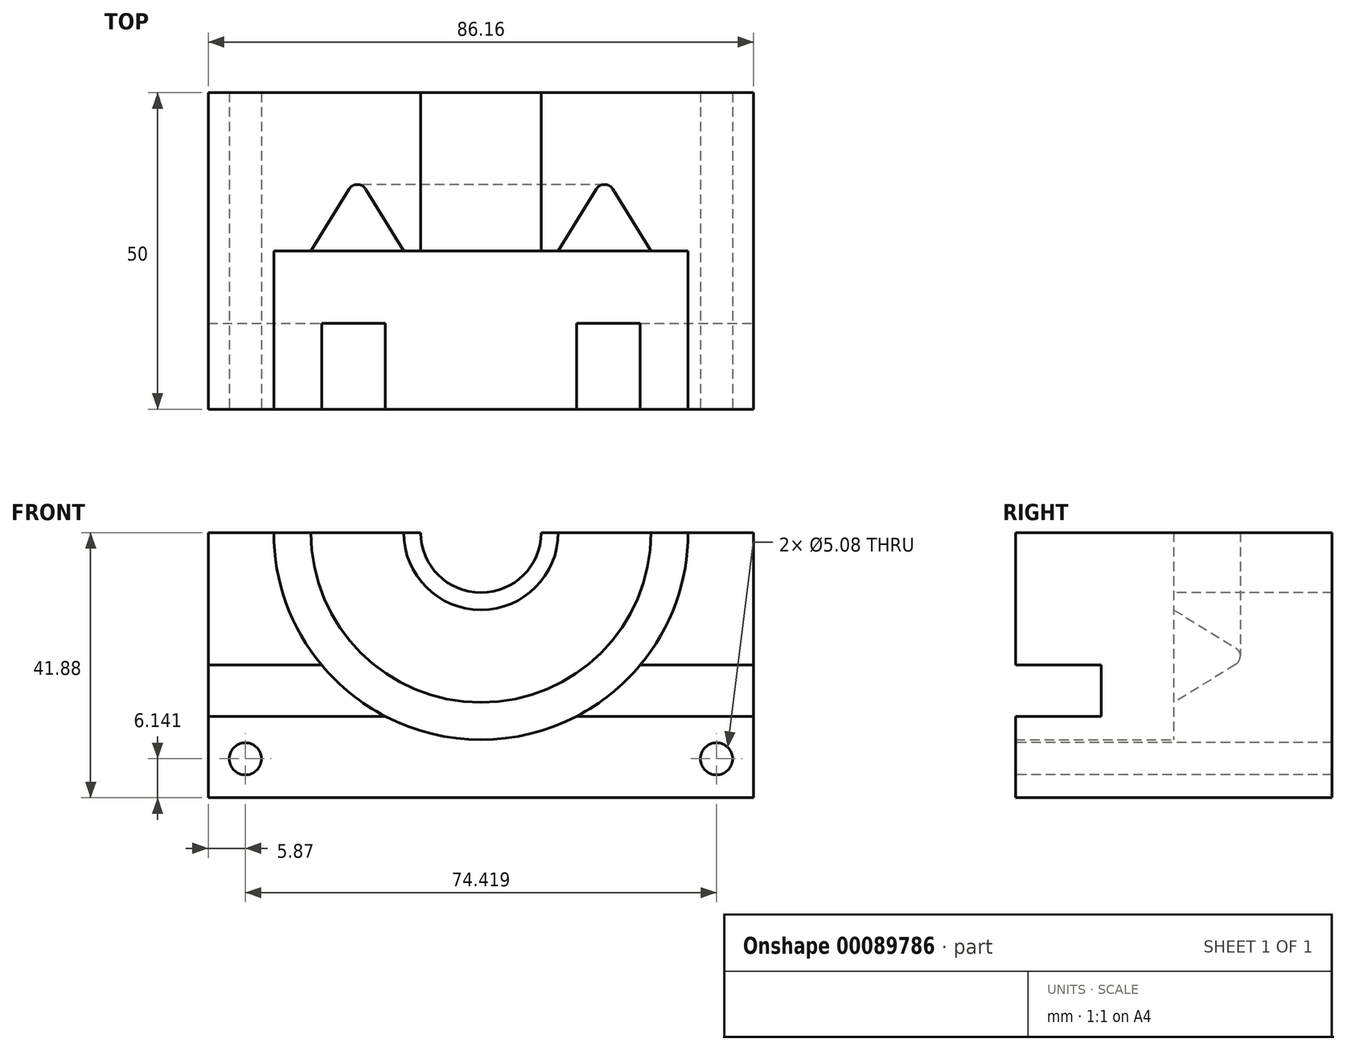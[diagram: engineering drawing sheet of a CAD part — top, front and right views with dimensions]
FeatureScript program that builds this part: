
annotation { "Feature Type Name" : "Feature", "Feature Type Description" : "" }
export const myFeature = defineFeature(function(context is Context, id is Id, definition is map)
    precondition{}
    {
        {
            var Q0;
            Q0=qCreatedBy(makeId("Front.planeOp"),FACE);
            var sketch = newSketch(context, id + "F0", { "sketchPlane" : qUnion([Q0])});
            skLineSegment(sketch, "E0", {"start": v(-43.08, 0) * mm, "end": v(0, 0) * mm});
            skLineSegment(sketch, "E1", {"start": v(0, 0) * mm, "end": v(43.08, 0) * mm});
            skLineSegment(sketch, "E2", {"start": v(43.08, 0) * mm, "end": v(43.08, 41.88) * mm});
            skLineSegment(sketch, "E3.MirrorCS", {"start": v(-43.08, 0) * mm, "end": v(-43.08, 41.88) * mm});
            skLineSegment(sketch, "E4", {"start": v(-43.08, 41.88) * mm, "end": v(43.08, 41.88) * mm});
            skSolve(sketch);
        }
        {
            var Q0;
            Q0=makeQuery(id+"F0.imprint","IMPRINT",FACE,{"disambiguationData":[TD([[makeQuery(id+"F0.imprint","IMPRINT",EDGE,{"derivedFrom":sQuery(id+"F0.wireOp",EDGE,"E0")}),1.0]])]});
            extrude(context, id + "F1", {"entities" : qUnion([Q0]), "endBound" : BoundingType.SYMMETRIC, "depth" : 50 * mm});
        }
        {
            var Q0;
            Q0=makeQuery(id+"F1.opExtrude","SWEPT_FACE",FACE,{"disambiguationData":[OSD([sQuery(id+"F0.wireOp",EDGE,"E4")])]});
            var sketch = newSketch(context, id + "F2", { "sketchPlane" : qUnion([Q0])});
            skLineSegment(sketch, "E5", {"start": v(-26.85, 0) * mm, "end": v(-19.53, 11.87) * mm});
            skLineSegment(sketch, "E6", {"start": v(-19.53, 11.87) * mm, "end": v(-12.2, 0) * mm});
            skLineSegment(sketch, "E7", {"start": v(-12.2, 0) * mm, "end": v(-26.85, 0) * mm});
            skLineSegment(sketch, "E8", {"start": v(0, 25) * mm, "end": v(0, -25) * mm});
            skSolve(sketch);
        }
        {
            var Q0;
            Q0=makeQuery(id+"F2.imprint","IMPRINT",FACE,{"disambiguationData":[TD([[makeQuery(id+"F2.imprint","IMPRINT",EDGE,{"derivedFrom":sQuery(id+"F2.wireOp",EDGE,"E5")}),-1.0]])]});
            var Q1;
            Q1=sQuery(id+"F2.wireOp",EDGE,"E8");
            revolve(context, id + "F3", {"operationType" : NewBodyOperationType.REMOVE, "entities" : qUnion([Q0]), "axis" : qUnion([Q1]), "revolveType" : RevolveType.FULL, "oppositeDirection" : true});
        }
        {
            var Q0;
            Q0=makeQuery(id+"F1.opExtrude","SWEPT_FACE",FACE,{"disambiguationData":[OSD([sQuery(id+"F0.wireOp",EDGE,"E4")])]});
            var sketch = newSketch(context, id + "F4", { "sketchPlane" : qUnion([Q0])});
            skLineSegment(sketch, "E9", {"start": v(-32.73, 0) * mm, "end": v(-32.73, -25) * mm});
            skLineSegment(sketch, "E10", {"start": v(-32.73, -25) * mm, "end": v(0, -25) * mm});
            skLineSegment(sketch, "E11", {"start": v(0, -25) * mm, "end": v(0, 0) * mm});
            skLineSegment(sketch, "E12", {"start": v(0, 0) * mm, "end": v(-32.73, 0) * mm});
            skSolve(sketch);
        }
        {
            var Q0;
            Q0 = qSketchRegion(id + "F4", true);
            var Q1;
            Q1=sQuery(id+"F4.wireOp",EDGE,"E11");
            revolve(context, id + "F5", {"operationType" : NewBodyOperationType.REMOVE, "entities" : qUnion([Q0]), "axis" : qUnion([Q1]), "revolveType" : RevolveType.FULL, "oppositeDirection" : true});
        }
        {
            var Q0;
            Q0=makeQuery(id+"F3.boolean.opBoolean","COPY",EDGE,{"derivedFrom":makeQuery(id+"F3.opRevolve","SWEPT_EDGE",EDGE,{"disambiguationData":[OSD([sQuery(id+"F2.wireOp",EDGE,"E5"),sQuery(id+"F2.wireOp",EDGE,"E6")])]})});
            fillet(context, id + "F6", {"entities" : qUnion([Q0]), "radius" : 1.52 * mm, "tangentPropagation" : true, "allowEdgeOverflow" : false});
        }
        {
            var Q0;
            Q0=makeQuery(id+"F1.opExtrude","SWEPT_FACE",FACE,{"disambiguationData":[OSD([sQuery(id+"F0.wireOp",EDGE,"E2")])]});
            var sketch = newSketch(context, id + "F7", { "sketchPlane" : qUnion([Q0])});
            skLineSegment(sketch, "E13", {"start": v(-25, 20.94) * mm, "end": v(-11.47, 20.94) * mm});
            skLineSegment(sketch, "E14", {"start": v(-11.47, 20.94) * mm, "end": v(-11.47, 12.85) * mm});
            skLineSegment(sketch, "E15", {"start": v(-11.47, 12.85) * mm, "end": v(-25, 12.85) * mm});
            skLineSegment(sketch, "E16", {"start": v(-25, 12.85) * mm, "end": v(-25, 20.94) * mm});
            skSolve(sketch);
        }
        {
            var Q0;
            Q0 = qSketchRegion(id + "F7", true);
            extrude(context, id + "F8", {"entities" : qUnion([Q0]), "operationType" : NewBodyOperationType.REMOVE, "endBound" : BoundingType.THROUGH_ALL, "oppositeDirection" : true, "depth" : 25.4 * mm});
        }
        {
            var Q0;
            Q0=makeQuery(id+"F1.opExtrude","SWEPT_FACE",FACE,{"disambiguationData":[OSD([sQuery(id+"F0.wireOp",EDGE,"E4")])]});
            var sketch = newSketch(context, id + "F9", { "sketchPlane" : qUnion([Q0])});
            skLineSegment(sketch, "E17", {"start": v(-9.5, 0) * mm, "end": v(-9.5, 25) * mm});
            skLineSegment(sketch, "E18", {"start": v(-9.5, 25) * mm, "end": v(0, 25) * mm});
            skLineSegment(sketch, "E19", {"start": v(0, 25) * mm, "end": v(0, 0) * mm});
            skLineSegment(sketch, "E20", {"start": v(0, 0) * mm, "end": v(-9.5, 0) * mm});
            skSolve(sketch);
        }
        {
            var Q0;
            Q0 = qSketchRegion(id + "F9", true);
            var Q1;
            Q1=sQuery(id+"F9.wireOp",EDGE,"E19");
            revolve(context, id + "F10", {"operationType" : NewBodyOperationType.REMOVE, "entities" : qUnion([Q0]), "axis" : qUnion([Q1]), "revolveType" : RevolveType.FULL, "oppositeDirection" : true});
        }
        {
            var Q0;
            {var subQ0=sQuery(id+"F0.wireOp",EDGE,"E3.MirrorCS");var subQ1=sQuery(id+"F0.wireOp",EDGE,"E2");var subQ2=sQuery(id+"F0.wireOp",EDGE,"E1");var subQ3=sQuery(id+"F0.wireOp",EDGE,"E0");Q0=makeQuery(id+"F8.boolean.opBoolean","SPLIT",FACE,{"disambiguationData":[TD([makeQuery(id+"F1.opExtrude","SWEPT_FACE",FACE,{"disambiguationData":[OSD([subQ3,subQ2])]}),makeQuery(id+"F1.opExtrude","SWEPT_FACE",FACE,{"disambiguationData":[OSD([subQ1])]}),makeQuery(id+"F1.opExtrude","SWEPT_FACE",FACE,{"disambiguationData":[OSD([subQ0])]}),makeQuery(id+"F5.boolean.opBoolean","COPY",FACE,{"derivedFrom":makeQuery(id+"F5.opRevolve","SWEPT_FACE",FACE,{"disambiguationData":[OSD([sQuery(id+"F4.wireOp",EDGE,"E9")])]})}),makeQuery(id+"F8.opExtrude","SWEPT_FACE",FACE,{"disambiguationData":[OSD([sQuery(id+"F7.wireOp",EDGE,"E15")])]})])],"derivedFrom":makeQuery(id+"F1.opExtrude","CAP_FACE",FACE,{"disambiguationData":[OSD([subQ3,subQ2,subQ1,subQ0,sQuery(id+"F0.wireOp",EDGE,"E4")])],"isStart":false})});}
            var sketch = newSketch(context, id + "F11", { "sketchPlane" : qUnion([Q0])});
            skPoint(sketch, "E21", {"position": v(-37.2, 6.14) * mm});
            skPoint(sketch, "E22.MirrorP", {"position": v(37.2, 6.14) * mm});
            skSolve(sketch);
        }
        {
            var Q0;
            Q0=sQuery(id+"F11.wireOp",VERTEX,"E21");
            var Q1;
            Q1=sQuery(id+"F11.wireOp",VERTEX,"E22.MirrorP");
            var Q2;
            Q2=makeQuery(id+"F1.opExtrude","SWEPT_BODY",BODY,{"disambiguationData":[OSD([sQuery(id+"F0.wireOp",EDGE,"E0"),sQuery(id+"F0.wireOp",EDGE,"E1"),sQuery(id+"F0.wireOp",EDGE,"E2"),sQuery(id+"F0.wireOp",EDGE,"E3.MirrorCS"),sQuery(id+"F0.wireOp",EDGE,"E4")])]});
            hole(context, id + "F12", {"style" : HoleStyle.SIMPLE, "endStyle" : HoleEndStyle.THROUGH, "holeDiameter" : 5.08 * mm, "locations" : qUnion([Q0, Q1]), "scope" : qUnion([Q2]), "isTappedThrough" : true});
        }
    });
